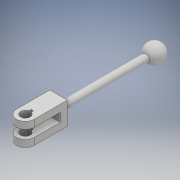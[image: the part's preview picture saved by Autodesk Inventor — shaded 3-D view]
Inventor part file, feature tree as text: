
AUTODESK INVENTOR PART (.ipt)
format: ipt  version: 2018 (Build 220112000, 112)  size: 162,816 bytes
history: native  units: mm
features: sketch x4, extrude x3, revolve x1, fillet x1, hole x1
ambient origin geometry x8: Origin, YZ Plane, XZ Plane, XY Plane, X Axis, Y Axis, Z Axis, Center Point
bodies: Solid1 (feature_tree)
feature tree (10):
  extrude  "Extrusion1"  Depth=4.0mm
  extrude  "Extrusion2"  Depth=5.0mm
  revolve  "Revolution1"  [1 undecoded]
  fillet  "Fillet1"  Radius=5.0mm
  hole  "Hole1"  [1 undecoded]
  extrude  "Extrusion3"  Depth=2.5mm
  sketch  "Sketch1"  dims[d0=4.0mm d1=20.0mm]
  sketch  "Sketch2"  dims[d2=4.0mm d3=5.0mm]
  sketch  "Sketch3"  dims[d4=10.0mm d5=0.0mm d6=4.0mm d7=5.0mm]
  sketch  "Sketch4"  dims[d8=6.5mm d9=50.0mm d10=0.0mm d11=2.5mm d12=0.0mm d13=10.0mm d14=90.0deg d15=5.0mm d30=10.0mm d31=10.0mm d18=5.5mm d19=6.0mm d20=4.0mm d21=2.0mm d22=90.0deg d23=8.0mm d24=0.0mm d25=1.35mm d26=0.675mm d27=1.35mm d28=50.0mm d29=0.0mm]
note: 2 required parameter values undecoded (feature->parameter linkage not recoverable at this tier; creation-order binding heuristic only, values carry confidence <= 0.55)